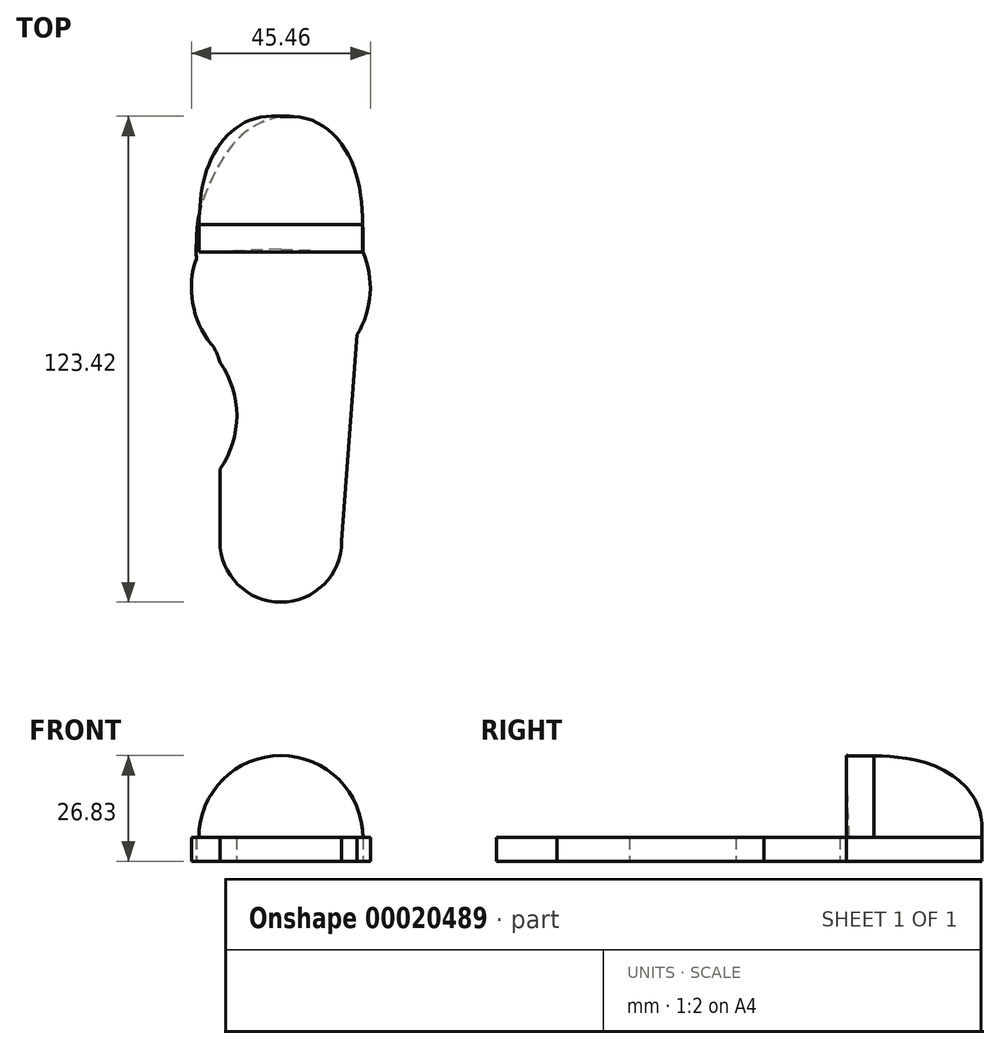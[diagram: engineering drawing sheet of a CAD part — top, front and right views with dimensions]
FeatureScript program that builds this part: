
annotation { "Feature Type Name" : "Feature", "Feature Type Description" : "" }
export const myFeature = defineFeature(function(context is Context, id is Id, definition is map)
    precondition{}
    {
        {
            var Q0;
            Q0=qCreatedBy(makeId("Top.planeOp"),FACE);
            var sketch = newSketch(context, id + "F0", { "sketchPlane" : qUnion([Q0])});
            skArc(sketch, "E0", {"start": v(-15.48, -31.89) * mm, "mid": v(0, -47.36) * mm, "end": v(15.48, -31.89) * mm});
            skLineSegment(sketch, "E1", {"start": v(15.48, -31.89) * mm, "end": v(19.38, 20.62) * mm});
            skLineSegment(sketch, "E2", {"start": v(-15.48, -31.89) * mm, "end": v(-15.48, -13.53) * mm});
            skArc(sketch, "E3", {"start": v(-15.48, -13.53) * mm, "mid": v(-11.18, 0) * mm, "end": v(-15.48, 13.53) * mm});
            skArc(sketch, "E4", {"start": v(19.38, 20.62) * mm, "mid": v(22.67, 30.93) * mm, "end": v(20.83, 41.6) * mm});
            skPoint(sketch, "E5.visualSharp", {"position": v(-15.48, 15.85) * mm});
            skFitSpline(sketch, "E6", {"points": [v(20.83, 41.6) * mm, v(18.44, 63.48) * mm, v(7.47, 75.21) * mm, v(-7.91, 72.9) * mm, v(-17.53, 60.21) * mm, v(-20.99, 49.83) * mm, v(-21.47, 39.97) * mm], "startDerivative": vector(0.71, 118.15) * mm, "endDerivative": vector(0.9, -59.13) * mm});
            skArc(sketch, "E7.trimOffspring", {"start": v(-21.47, 39.97) * mm, "mid": v(-22.4, 28.6) * mm, "end": v(-17.69, 18.22) * mm});
            skFitSpline(sketch, "E8", {"points": [v(-15.48, 13.53) * mm, v(-16.56, 16.93) * mm], "startDerivative": vector(-1.09, 3.4) * mm, "endDerivative": vector(-1.09, 3.4) * mm});
            skArc(sketch, "E9.filletArc", {"start": v(-15.94, 14.98) * mm, "mid": v(-16.66, 16.68) * mm, "end": v(-17.69, 18.22) * mm});
            skSolve(sketch);
        }
        {
            var Q0;
            Q0=makeQuery(id+"F0.imprint","IMPRINT",FACE,{"disambiguationData":[TD([[makeQuery(id+"F0.imprint","IMPRINT",EDGE,{"derivedFrom":sQuery(id+"F0.wireOp",EDGE,"E0")}),1.0]])]});
            extrude(context, id + "F1", {"entities" : qUnion([Q0]), "endBound" : BoundingType.SYMMETRIC, "depth" : 6 * mm});
        }
        {
            var Q0;
            Q0=makeQuery(id+"F1.opExtrude","CAP_FACE",FACE,{"disambiguationData":[OSD([sQuery(id+"F0.wireOp",EDGE,"E0"),sQuery(id+"F0.wireOp",EDGE,"E1"),sQuery(id+"F0.wireOp",EDGE,"E2"),sQuery(id+"F0.wireOp",EDGE,"E3"),sQuery(id+"F0.wireOp",EDGE,"E4"),sQuery(id+"F0.wireOp",EDGE,"E6"),sQuery(id+"F0.wireOp",EDGE,"E7.trimOffspring"),sQuery(id+"F0.wireOp",EDGE,"E8"),sQuery(id+"F0.wireOp",EDGE,"E9.filletArc")])],"isStart":false});
            var sketch = newSketch(context, id + "F2", { "sketchPlane" : qUnion([Q0])});
            skLineSegment(sketch, "E10", {"start": v(0, 94.7) * mm, "end": v(0, 22.74) * mm, "construction": true});
            skLineSegment(sketch, "E11", {"start": v(0, 75.9) * mm, "end": v(0, 42.3) * mm});
            skLineSegment(sketch, "E12", {"start": v(0, 42.3) * mm, "end": v(20.83, 41.6) * mm});
            skLineSegment(sketch, "E13.0.0", {"start": v(-15.48, -13.53) * mm, "end": v(-15.48, -31.89) * mm});
            skArc(sketch, "E13.0.1", {"start": v(-15.48, -31.89) * mm, "mid": v(0, -47.36) * mm, "end": v(15.48, -31.89) * mm});
            skLineSegment(sketch, "E13.0.2", {"start": v(15.48, -31.89) * mm, "end": v(19.38, 20.62) * mm});
            skArc(sketch, "E13.0.3", {"start": v(19.38, 20.62) * mm, "mid": v(22.67, 30.93) * mm, "end": v(20.83, 41.6) * mm});
            skFitSpline(sketch, "E13.0.4", {"points": [v(20.83, 41.6) * mm, v(20.88, 49.6) * mm, v(20.89, 63.57) * mm, v(8.65, 77.94) * mm, v(-9.5, 74.95) * mm, v(-17.88, 60.33) * mm, v(-21.53, 50.42) * mm, v(-21.5, 42.65) * mm, v(-21.47, 39.97) * mm]});
            skArc(sketch, "E13.0.5", {"start": v(-21.47, 39.97) * mm, "mid": v(-22.4, 28.6) * mm, "end": v(-17.69, 18.22) * mm});
            skArc(sketch, "E13.0.6", {"start": v(-17.69, 18.22) * mm, "mid": v(-16.66, 16.68) * mm, "end": v(-15.94, 14.98) * mm});
            skFitSpline(sketch, "E13.0.7", {"points": [v(-16.56, 16.93) * mm, v(-16.2, 15.8) * mm, v(-15.84, 14.66) * mm, v(-15.48, 13.53) * mm]});
            skArc(sketch, "E13.0.8", {"start": v(-15.48, 13.53) * mm, "mid": v(-11.18, 0) * mm, "end": v(-15.48, -13.53) * mm});
            skSolve(sketch);
        }
        {
            var Q0;
            Q0=makeQuery(id+"F2.imprint","IMPRINT",FACE,{"disambiguationData":[TD([[makeQuery(id+"F2.imprint","IMPRINT",EDGE,{"derivedFrom":sQuery(id+"F2.wireOp",EDGE,"E11")}),1.0]])]});
            var Q1;
            Q1=sQuery(id+"F2.wireOp",EDGE,"E10");
            revolve(context, id + "F3", {"operationType" : NewBodyOperationType.ADD, "entities" : qUnion([Q0]), "axis" : qUnion([Q1]), "revolveType" : RevolveType.ONE_DIRECTION, "angle" : 180 * degree});
        }
    });
